# Revit family: IS_Gusto_BD414_BIM_NL
name_source: partatom
category: Plumbing Fixtures
units: mm (PartAtom-declared; Revit-internal decimal feet)

## family parameters
Always vertical = No
Cut with Voids When Loaded = No
OmniClass Number = 23.45.55.17
OmniClass Title = Mixing Faucets
Part Type = Normal
Room Calculation Point = No
Round Connector Dimension = Use Diameter
Shared = No
Work Plane-Based = No

## types (5) — shared parameters
Accessories = https://www.idealstandard.nl
Afmetingen = 115 x 277 x 456 mm
AfstandsEenheid = Millimeter
AreaUnits = millimetres
AssetType = Fixed
Auteur = Ideal Standard
BIMObjectName = IS_IdealStandard_Sinktaps_Gusto_BD414
BIMobject category = Taps & Mixers
BIMobject category code = sanitary-taps-mixers
BIMobject main category = Sanitary
BIMobject main category code = sanitary
Bedieningkraan = Einhebel
Bedieningkraanwerk = Einhebel
Beschrijvinggarantie = Herstellergarantie
Bestanddelen = https://www.idealstandard.nl
BimObjectNaam = IS_IdealStandard_Sinktaps_Gusto_BD414
Brand = Ideal Standard
Brand url = http://www.idealstandard.nl
Breedte = 114.689484
Category = Taps & Mixers
ConnectionType = Plumbing
CurrencyUnit = €
CurrentRevision = 1
Date of publishing = 19/08/2022
Diepte = 277 mm
DurationUnit = Years
DuurEenheid = Jahre
Edition number = 1
ExpectedLife = 5
FaucetFunction = Sink Mixer
FaucetOperation = Single Lever Sink Mixer
FaucetType = Sink Mixer
Functiekraanwerk = Küchenmischer
GTIN code = https://3800861108801
Garantieunits = Jahre
Help = https://www.idealstandard.nl
Hoogte = 455.661671986338
Hulp = https://www.idealstandard.nl
IFC Classification = Sanitary Terminal
IfcExportAs = IfcValveType
IfcExportType = FAUCET
Installatieinstructies = https://www.idealstandard.nl
Installation instructions = https://www.idealstandard.nl
InstallationInstructions = https://www.idealstandard.nl
Lengte = 277 mm
LinearUnits = millimetres
MaintenanceInformation = https://www.idealstandard.nl
Manufacturer = Ideal Standard
Manufacturer name = Ideal Standard
ManufacturerURL = http://www.idealstandard.nl
Masterformat 2014 Code = 22 41 16.16
Masterformat 2014 Description = Residential Sink
Materiaal = Messing
Material = Brass
Material main = Brass
Merk = Ideal Standard
NBS Reference Code = 45-35-70/345
NBS Reference Description = Water supply fittings for sinks
Name = Sinktaps_Gusto_BD414_IdealStandard
NettWeight = 3.23 Kg
Nettogewicht = 3.23
NominalDepth = 277 mm
NominalHeight = 456 mm
NominalLength = 277 mm
NominalWidth = 115 mm
Normen = Sinktaps_Gusto_BD414_IdealStandard
OmniClass Code = 23-31 11 00
OmniClass Description = Faucets
OppervlakteEenheid = Millimeter
PredefinedType = Taps & Mixers
Product Guid = 717b89b9-3f78-499c-8208-63b433153ff6
Product SKU = BD414
Product certification = https://www.idealstandard.nl
Product data url = https://bimobject.com
Product family = Gusto
Product group = Taps & Mixers
Product name = GUSTO SINK MIXER C SPOUT P/D 1 FUNTION BLUE START
Product url = https://www.idealstandard.nl
ProductInformation = https://www.idealstandard.nl
Productinformatie = https://www.idealstandard.nl
QR code = http://bimobject.com
Revisie = 1
Shape = Cylindrical
Size = 115 x 277 x 456 mm
Space = Internal
SpareParts = https://www.idealstandard.nl
Technical description = https://www.idealstandard.nl
Telefoonnummer = (0228) 521-580
Toepassing = Küchenmischer
Type Comments = Plumbing
Typeconnectie = Installation
Typekraanwerk = Einhebelmischer
UNSPSC Code = 301815
URL = https://www.idealstandard.nl
Uniclass 2015 Code = Pr_40_20_87_82
Uniclass 2015 Name = Sink manual water supply sets
Uniclass2015Beschrijving = Sink manual water supply sets
Uniclass2015Code = Pr_40_20_87_84
Uniclass2015Referentie = Pr_40_20_87_82
Uniclass2015Title = Sink taps
Uniclass2015Version = v1.26
Urlproducent = https://www.idealstandard.nl
ValutaEenheid = Euro
Versie = 1
Version = 1
VolumeUnits = Liters
Volumeunits = Liter
Vorm = Zylinder
WRASURL = https://www.wrasapprovals.co.uk
WarrantyDescription = manufacturer warranty
WarrantyDurationParts = 5
WarrantyDurationUnit = Years
WarrantyStartDate = 19/08/2022
Weight Net (Kg) = 3.23
Wisselstukken = https://www.idealstandard.nl
Youtube clip = https://www.youtube.com
zero-valued in all types: BrutoGewicht, Cost, Vervangingskosten

## per-type parameters (varying)
| type | Afwerking | Artikelnummer | Artikelomschrijving | Artikelreferentie | BarCode | Barcode | BeschrijvingBovenkantKraan | Color | Description | Eigenschappen | FaucetTopDescription | Features | Finish | Kleur | MainColor | Model | ModelNumber | ModelReference |
| BD414A5 - Gusto sink mixer C spout p/d 1 funtion blue start - Magnetic Grey | Magnetisches Grau | BD414A5 | Gusto Spültischmischer C Auslauf p/d 1 funtion blue start - Magnetic Grey | Gusto Spültischmischer C Auslauf p/d 1 funtion blue start - Magnetic Grey | 3800861109105 | 3800861109105 | C Auslauf | Magnetic Grey | Gusto sink mixer C spout p/d 1 funtion blue start - Magnetic Grey | Spültischmischer C Auslauf p/d 1 funtion blue start - Magnetic Grey | C spout | Sink mixer C spout p/d 1 funtion blue start - Magnetic Grey | Magnetic Grey | Magnetisches Grau | Magnetic Grey | BD414A5 | BD414A5 | Gusto sink mixer C spout p/d 1 funtion blue start |
| BD414AA - Gusto slim sink rim mounted mxr p/d 1 funtion blue start - Chrome | Chrom | BD414AA | Gusto schmales Spülbecken mit Randmontage mxr p/d 1 Funktion blauer Start - Chrom | Gusto schmales Spülbecken mit Randmontage mxr p/d 1 Funktion blauer Start - Chrom | 3800861108634 | 3800861108634 | 1 Funktion | Chrome | Gusto slim sink rim mounted mxr p/d 1 funtion blue start - Chrome | Slim Sink randmontiertes mxr p/d 1 funtion blue start - Chrom | Single lever | Slim Sink rim mounted mxr p/d 1 funtion blue start - Chrome | Chrome | Chrom | Chrome | BD414AA | BD414AA | Gusto slim sink rim mounted mxr p/d 1 funtion blue start |
| BD414GN - Gusto sink mixer C spout p/d 1 funtion blue start - Silver | Silber | BD414GN | Gusto Spültischmischer C Auslauf p/d 1 funtion blue start - Silver | Gusto Spültischmischer C Auslauf p/d 1 funtion blue start - Silver | 3800861108795 | 3800861108795 | C Auslauf | Silver | Gusto sink mixer C spout p/d 1 funtion blue start - Silver | Spültischmischer C Auslauf p/d 1 funtion blue start - Silver | C spout | Sink mixer C spout p/d 1 funtion blue start - Silver | Silver | Silber | Silver | BD414GN | BD414GN | Gusto sink mixer C spout p/d 1 funtion blue start |
| BD414J4 - Gusto sink mixer C spout p/d 1 funtion blue start - Brushed Copper | Gebürstetes Kupfer | BD414J4 | Gusto Spültischmischer C Auslauf p/d 1 funtion blue start - Brushed Copper | Gusto Spültischmischer C Auslauf p/d 1 funtion blue start - Brushed Copper | 3800861109266 | 3800861109266 | C Auslauf | Brushed Copper | Gusto sink mixer C spout p/d 1 funtion blue start - Brushed Copper | Spültischmischer C Auslauf p/d 1 funtion blue start - Brushed Copper | C spout | Sink mixer C spout p/d 1 funtion blue start - Brushed Copper | Brushed Copper | Gebürstetes Kupfer | Brushed Copper | BD414J4 | BD414J4 | Gusto sink mixer C spout p/d 1 funtion blue start |
| BD414A2 - Gusto sink mixer C spout p/d 1 funtion blue start - BrushedGold | Gebürstetes Gold | BD414A2 | Gusto Spültischmischer C Auslauf p/d 1 funtion blue start - BrushedGold | Gusto Spültischmischer C Auslauf p/d 1 funtion blue start - BrushedGold | 3800861108801 | 3800861108801 | C Auslauf | BrushedGold | Gusto sink mixer C spout p/d 1 funtion blue start - BrushedGold | Spültischmischer C Auslauf p/d 1 funtion blue start - BrushedGold | C spout | Sink mixer C spout p/d 1 funtion blue start - BrushedGold | BrushedGold | Gebürstetes Gold | BrushedGold | BD414A2 | BD414A2 | Gusto sink mixer C spout p/d 1 funtion blue start |

## geometry (parser evidence)
native form markers: Sweep x2
no freeform markers — native parametric forms only
